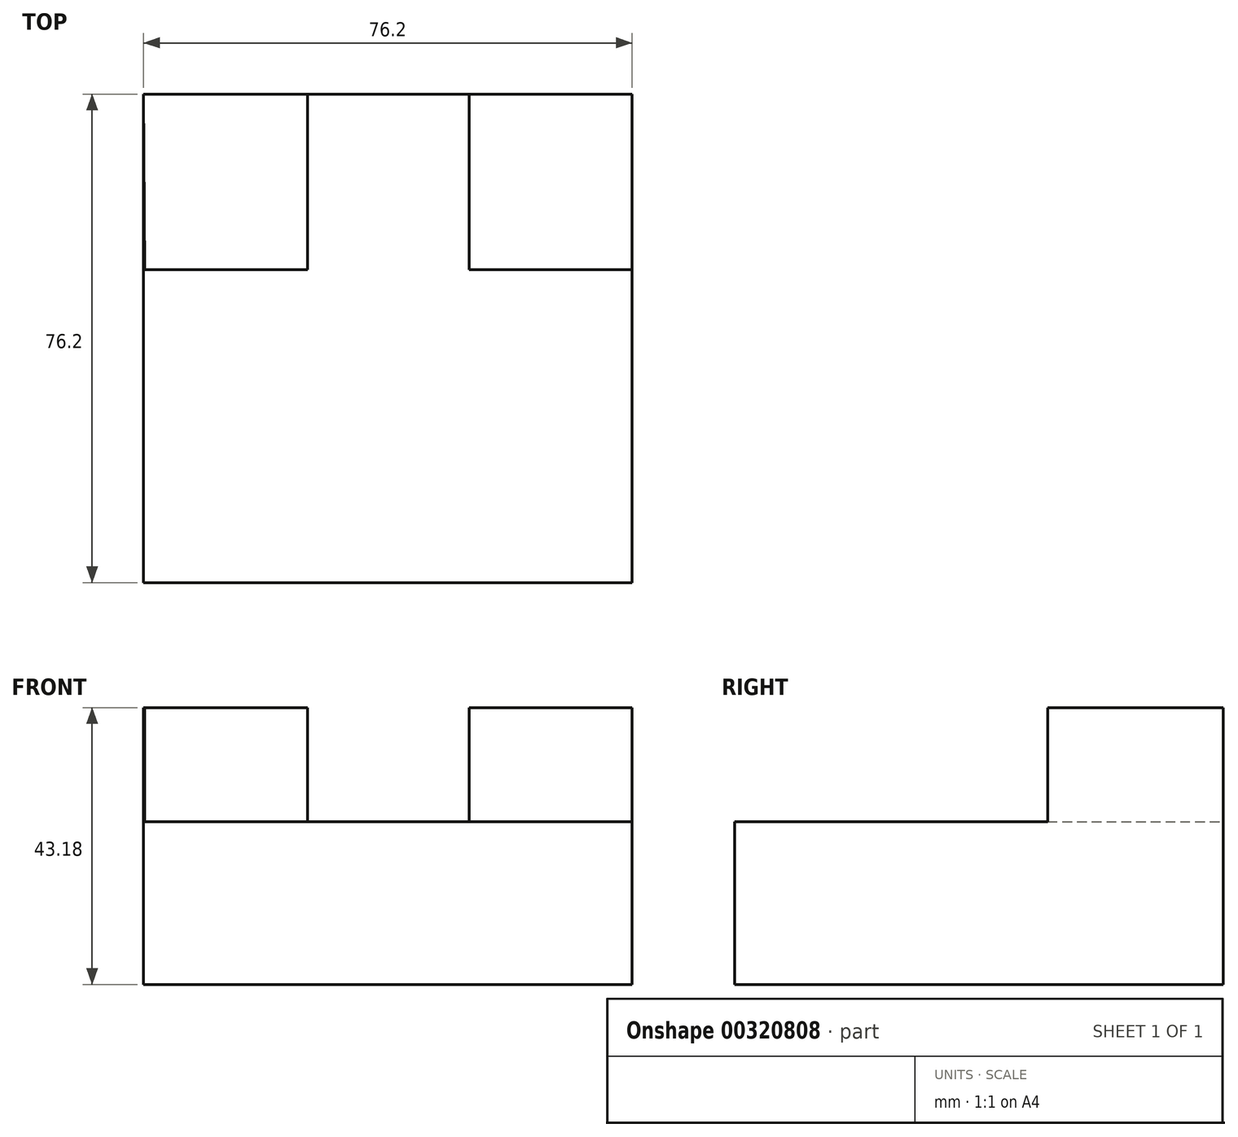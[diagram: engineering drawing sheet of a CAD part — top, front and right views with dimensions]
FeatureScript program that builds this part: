
annotation { "Feature Type Name" : "Feature", "Feature Type Description" : "" }
export const myFeature = defineFeature(function(context is Context, id is Id, definition is map)
    precondition{}
    {
        {
            var Q0;
            Q0=qCreatedBy(makeId("Front.planeOp"),FACE);
            var sketch = newSketch(context, id + "F0", { "sketchPlane" : qUnion([Q0])});
            skLineSegment(sketch, "E0", {"start": v(-54.66, -23.63) * mm, "end": v(21.54, -23.63) * mm});
            skLineSegment(sketch, "E1", {"start": v(21.54, -23.63) * mm, "end": v(21.54, 1.77) * mm});
            skLineSegment(sketch, "E2", {"start": v(21.54, 1.77) * mm, "end": v(-54.66, 1.77) * mm});
            skLineSegment(sketch, "E3", {"start": v(-54.66, 1.77) * mm, "end": v(-54.66, -23.63) * mm});
            skSolve(sketch);
        }
        {
            var Q0;
            Q0 = qSketchRegion(id + "F0", true);
            extrude(context, id + "F1", {"entities" : qUnion([Q0]), "depth" : 76.2 * mm});
        }
        {
            var Q0;
            Q0=makeQuery(id+"F1.opExtrude","SWEPT_FACE",FACE,{"disambiguationData":[OSD([sQuery(id+"F0.wireOp",EDGE,"E2")])]});
            var sketch = newSketch(context, id + "F2", { "sketchPlane" : qUnion([Q0])});
            skLineSegment(sketch, "E4", {"start": v(-54.47, -27.4) * mm, "end": v(-29.07, -27.4) * mm});
            skLineSegment(sketch, "E5", {"start": v(-29.07, -27.4) * mm, "end": v(-29.07, 0) * mm});
            skLineSegment(sketch, "E6", {"start": v(-29.07, 0) * mm, "end": v(-54.66, 0) * mm});
            skLineSegment(sketch, "E7", {"start": v(-54.66, 0) * mm, "end": v(-54.47, -27.4) * mm});
            skSolve(sketch);
        }
        {
            var Q0;
            Q0 = qSketchRegion(id + "F2", true);
            extrude(context, id + "F3", {"entities" : qUnion([Q0]), "operationType" : NewBodyOperationType.ADD, "depth" : 17.78 * mm});
        }
        {
            var Q0;
            Q0=makeQuery(id+"F1.opExtrude","SWEPT_FACE",FACE,{"disambiguationData":[OSD([sQuery(id+"F0.wireOp",EDGE,"E2")])]});
            var sketch = newSketch(context, id + "F4", { "sketchPlane" : qUnion([Q0])});
            skLineSegment(sketch, "E8", {"start": v(21.54, -27.4) * mm, "end": v(-3.86, -27.4) * mm});
            skLineSegment(sketch, "E9", {"start": v(-3.86, -27.4) * mm, "end": v(-3.86, 0) * mm});
            skLineSegment(sketch, "E10", {"start": v(-3.86, 0) * mm, "end": v(21.54, 0) * mm});
            skLineSegment(sketch, "E11", {"start": v(21.54, 0) * mm, "end": v(21.54, -27.4) * mm});
            skSolve(sketch);
        }
        {
            var Q0;
            Q0 = qSketchRegion(id + "F4", true);
            extrude(context, id + "F5", {"entities" : qUnion([Q0]), "operationType" : NewBodyOperationType.ADD, "depth" : 17.78 * mm});
        }
    });
